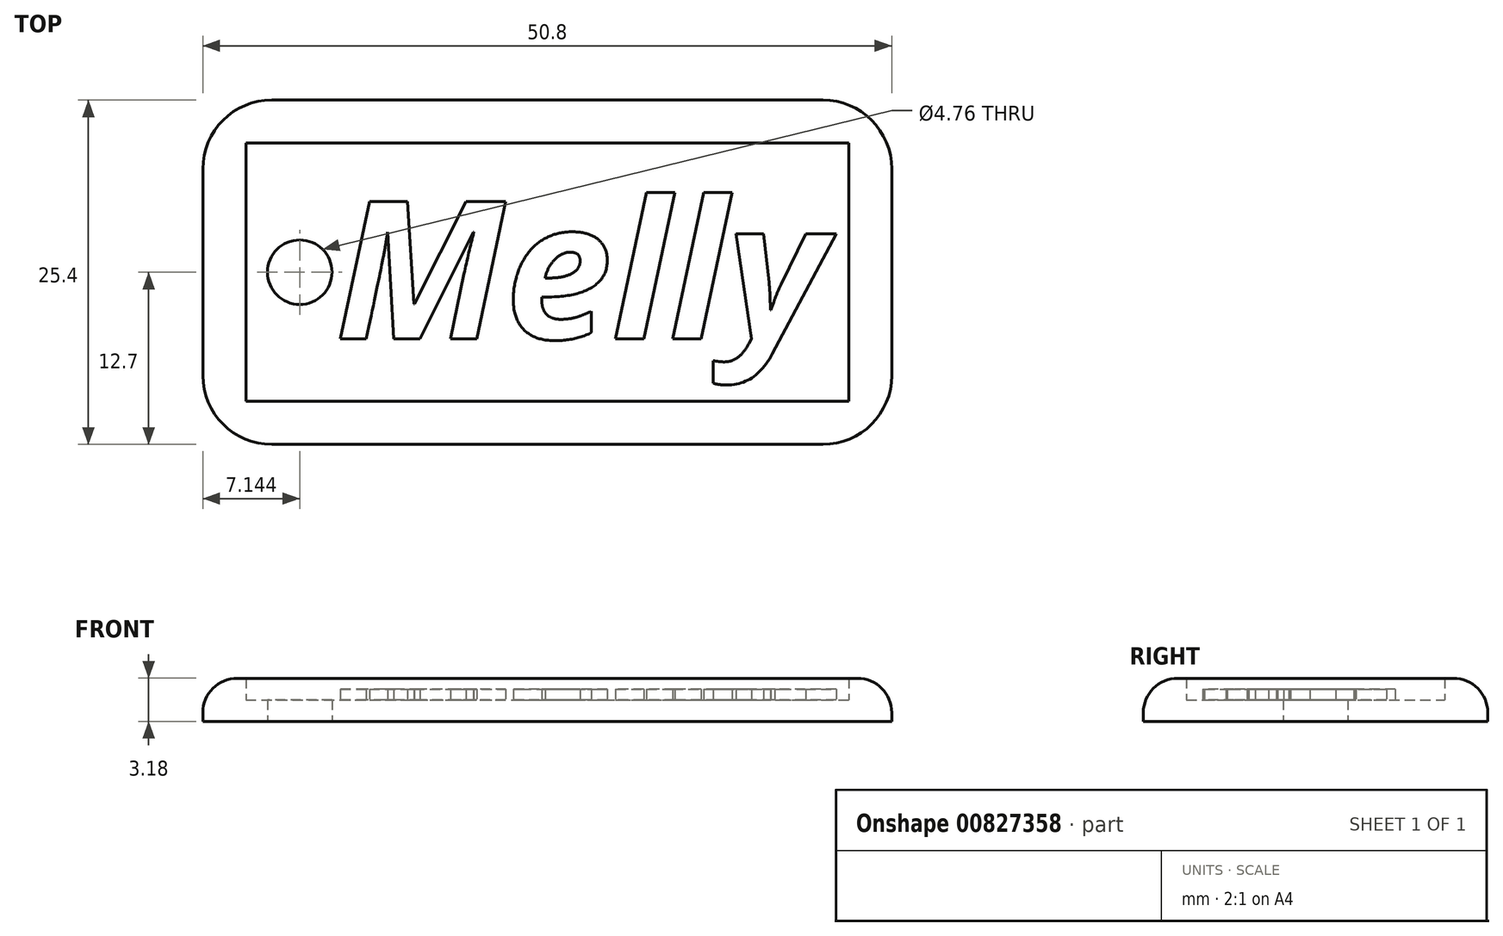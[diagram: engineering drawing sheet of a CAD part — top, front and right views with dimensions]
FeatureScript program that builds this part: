
annotation { "Feature Type Name" : "Feature", "Feature Type Description" : "" }
export const myFeature = defineFeature(function(context is Context, id is Id, definition is map)
    precondition{}
    {
        {
            var Q0;
            Q0=qCreatedBy(makeId("Top.planeOp"),FACE);
            var sketch = newSketch(context, id + "F0", { "sketchPlane" : qUnion([Q0])});
            skLineSegment(sketch, "E0.bottom", {"start": v(0, 0) * mm, "end": v(50.8, 0) * mm});
            skLineSegment(sketch, "E0.top", {"start": v(0, 25.4) * mm, "end": v(50.8, 25.4) * mm});
            skLineSegment(sketch, "E0.left", {"start": v(0, 0) * mm, "end": v(0, 25.4) * mm});
            skLineSegment(sketch, "E0.right", {"start": v(50.8, 0) * mm, "end": v(50.8, 25.4) * mm});
            skCircle(sketch, "E1", {"center": v(7.14, 12.7) * mm, "radius": 2.38 * mm});
            skPoint(sketch, "E1.centerSnap0", {"position": v(0, 12.7) * mm});
            skLineSegment(sketch, "E2.0", {"start": v(3.18, 22.23) * mm, "end": v(47.62, 22.23) * mm});
            skLineSegment(sketch, "E2.1", {"start": v(3.18, 3.18) * mm, "end": v(3.18, 22.22) * mm});
            skLineSegment(sketch, "E2.2", {"start": v(3.18, 3.18) * mm, "end": v(47.62, 3.18) * mm});
            skLineSegment(sketch, "E2.3", {"start": v(47.62, 3.18) * mm, "end": v(47.62, 22.23) * mm});
            skSolve(sketch);
        }
        {
            var Q0;
            Q0=makeQuery(id+"F0.imprint","IMPRINT",FACE,{"disambiguationData":[TD([[makeQuery(id+"F0.imprint","IMPRINT",EDGE,{"derivedFrom":sQuery(id+"F0.wireOp",EDGE,"E1")}),-1.0]])]});
            extrude(context, id + "F1", {"entities" : qUnion([Q0]), "depth" : 1.59 * mm, "offsetDistance" : 25.4 * mm});
        }
        {
            var Q0;
            Q0 = qSketchRegion(id + "F0", true);
            extrude(context, id + "F2", {"entities" : qUnion([Q0]), "operationType" : NewBodyOperationType.ADD, "depth" : 3.17 * mm, "offsetDistance" : 25.4 * mm});
        }
        {
            var Q0;
            Q0=makeQuery(id+"F2.opExtrude","SWEPT_EDGE",EDGE,{"disambiguationData":[OSD([sQuery(id+"F0.wireOp",EDGE,"E0.bottom"),sQuery(id+"F0.wireOp",EDGE,"E0.left")])]});
            var Q1;
            Q1=makeQuery(id+"F2.opExtrude","SWEPT_EDGE",EDGE,{"disambiguationData":[OSD([sQuery(id+"F0.wireOp",EDGE,"E0.bottom"),sQuery(id+"F0.wireOp",EDGE,"E0.right")])]});
            var Q2;
            Q2=makeQuery(id+"F2.opExtrude","SWEPT_EDGE",EDGE,{"disambiguationData":[OSD([sQuery(id+"F0.wireOp",EDGE,"E0.top"),sQuery(id+"F0.wireOp",EDGE,"E0.right")])]});
            var Q3;
            Q3=makeQuery(id+"F2.opExtrude","SWEPT_EDGE",EDGE,{"disambiguationData":[OSD([sQuery(id+"F0.wireOp",EDGE,"E0.top"),sQuery(id+"F0.wireOp",EDGE,"E0.left")])]});
            fillet(context, id + "F3", {"entities" : qUnion([Q0, Q1, Q2, Q3]), "radius" : 5.08 * mm, "tangentPropagation" : true, "allowEdgeOverflow" : false});
        }
        {
            var Q0;
            Q0=makeQuery(id+"F2.opExtrude","CAP_EDGE",EDGE,{"disambiguationData":[OSD([sQuery(id+"F0.wireOp",EDGE,"E0.bottom")])],"isStart":false});
            fillet(context, id + "F4", {"entities" : qUnion([Q0]), "radius" : 2.54 * mm, "tangentPropagation" : true, "allowEdgeOverflow" : false});
        }
        {
            var Q0;
            Q0=makeQuery(id+"F1.opExtrude","CAP_FACE",FACE,{"disambiguationData":[OSD([sQuery(id+"F0.wireOp",EDGE,"E1"),sQuery(id+"F0.wireOp",EDGE,"E2.0"),sQuery(id+"F0.wireOp",EDGE,"E2.1"),sQuery(id+"F0.wireOp",EDGE,"E2.2"),sQuery(id+"F0.wireOp",EDGE,"E2.3")])],"isStart":false});
            var sketch = newSketch(context, id + "F5", { "sketchPlane" : qUnion([Q0])});
            skText(sketch, "E3", { "text": "Melly", "fontName": "OpenSans-BoldItalic.ttf"});
            const initialGuessF5  = {"E3": [0.00978, 0.00779, 1, 0, 0.01022]};
            skSetInitialGuess(sketch, initialGuessF5);
            skSolve(sketch);
        }
        {
            var Q0;
            Q0 = qSketchRegion(id + "F5", true);
            extrude(context, id + "F6", {"entities" : qUnion([Q0]), "operationType" : NewBodyOperationType.ADD, "depth" : 0.8 * mm, "offsetDistance" : 25.4 * mm});
        }
    });
